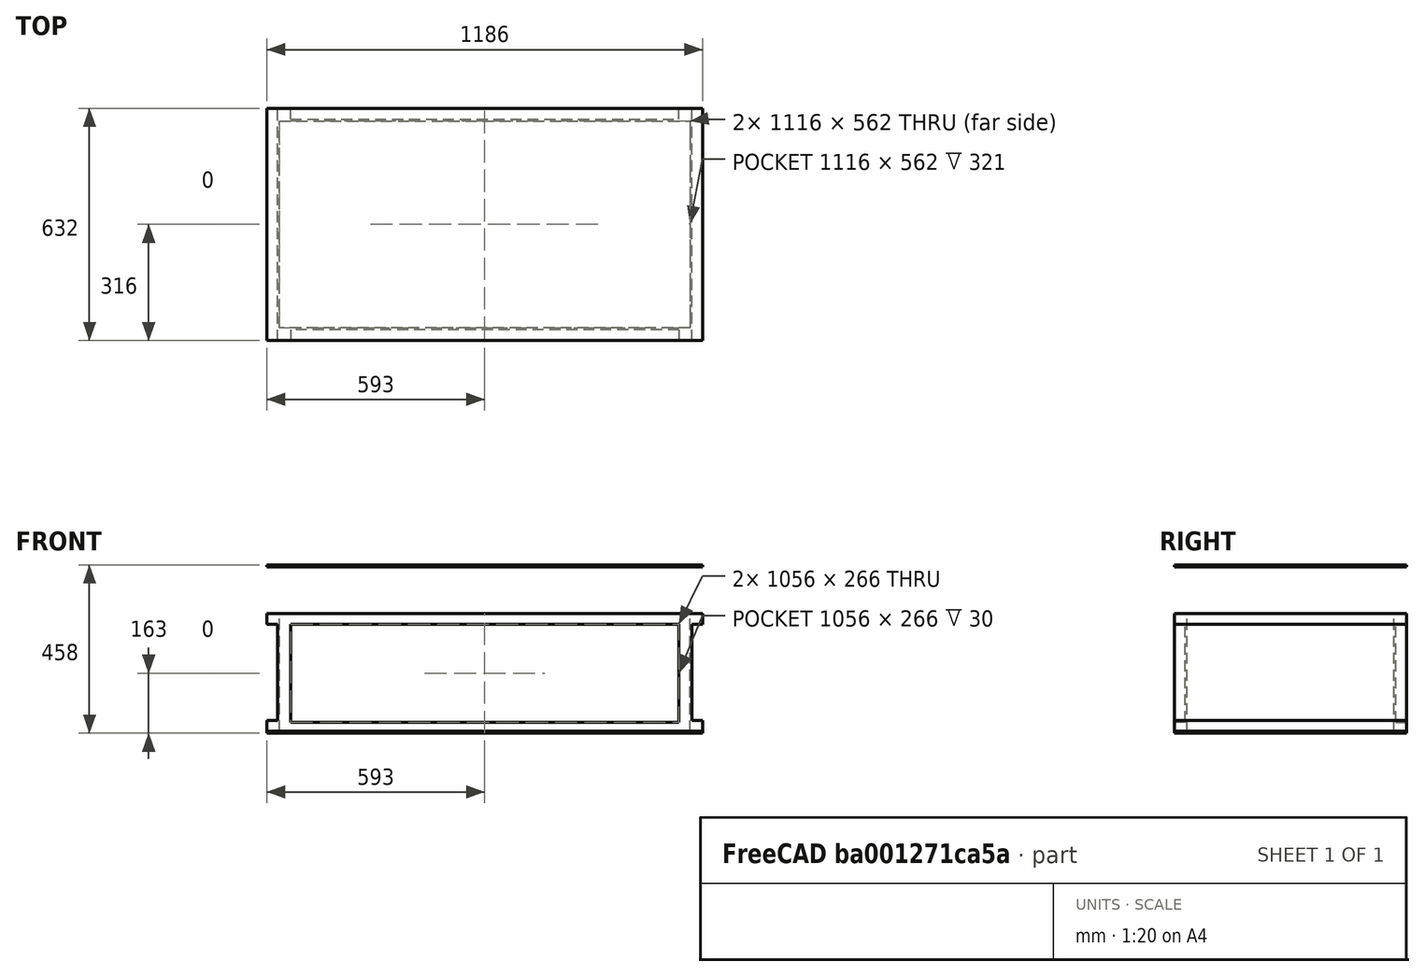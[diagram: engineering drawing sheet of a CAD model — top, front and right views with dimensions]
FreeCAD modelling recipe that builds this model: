
FCSTD DOCUMENT  (FreeCAD 0.20R)
Label: boite_lightcon_C231999
License: All rights reserved
LicenseURL: http://en.wikipedia.org/wiki/All_rights_reserved
objects: TechDraw::DrawViewDimension×11, Sketcher::SketchObject×5, PartDesign::Pocket×3, PartDesign::Pad×2, PartDesign::Mirrored×2, PartDesign::Body×2, TechDraw::DrawViewPart×2, TechDraw::DrawViewSection×2, Spreadsheet::Sheet×1, TechDraw::DrawSVGTemplate×1, PartDesign::Plane×1, Part::FeaturePython×1, TechDraw::DrawPage×1
note: 21 computed .brp shape members not serialized (recipe doc carries the construction recipe); baked Part::Feature solids carry a one-line shape summary decoded from their .brp

FEATURE [Sketcher::SketchObject] Sketch  label="extBox"
  FullyConstrained = true
  MapMode = 5
  Support = -> [XY_Plane]
  expr: Constraints[8] = Spreadsheet.extboxwidth
  expr: Constraints[9] = Spreadsheet.extboxlength
  sketch-geometry (4):
    g0: LineSegment StartX=-593 StartY=316 StartZ=0 EndX=593 EndY=316 EndZ=0
    g1: LineSegment StartX=593 StartY=316 StartZ=0 EndX=593 EndY=-316 EndZ=0
    g2: LineSegment StartX=593 StartY=-316 StartZ=0 EndX=-593 EndY=-316 EndZ=0
    g3: LineSegment StartX=-593 StartY=-316 StartZ=0 EndX=-593 EndY=316 EndZ=0
  constraints (10):
    c: Coincident(g0,g1)
    c: Coincident(g1,g2)
    c: Coincident(g2,g3)
    c: Coincident(g3,g0)
    c: Horizontal(g2)
    c: Vertical(g3)
    c: Symmetric(g0,g0,g-2)
    c: Symmetric(g0,g1,g-1)
    c: DistanceY(g3,g3) = 632
    c: DistanceX(g0,g0) = 1186
FEATURE [Spreadsheet::Sheet] Spreadsheet  label="dim"
  cells = A1=Braces thick; B1(Bracesthick)==30mm; A2=panel thick; B2(panelthick)==5mm; A3=ext box height; B3(extboxheight)==326mm; A4=ext box length; B4(extboxlength)==1186mm; A5=int box width; B5(intboxwidth)==562mm; A6=int box height; B6(intboxheight)==extboxheight - panelthick; A7=ext box width; B7(extboxwidth)==intboxwidth + 2 * panelthick + 2 * Bracesthick; A8=int box length; B8(intboxlength)==extboxlength - 2 * Bracesthick - 2 * panelthick
FEATURE [PartDesign::Pad] Pad
  Direction = (0,0,1)
  Length = 326
  Length2 = 10
  Profile = -> Sketch
  ReferenceAxis = -> Sketch [N_Axis]
  Type = 0
  expr: Length = Spreadsheet.extboxheight
FEATURE [Sketcher::SketchObject] Sketch001
  FullyConstrained = true
  MapMode = 5
  Placement = pos=(0,0,0) rot=(1,0,0;1.5708rad)
  Support = -> [XZ_Plane]
  expr: Constraints[10] = Spreadsheet.extboxlength / 2
  expr: Constraints[11] = Spreadsheet.Bracesthick
  expr: Constraints[8] = Spreadsheet.extboxheight - Spreadsheet.panelthick - 2 * Spreadsheet.Bracesthick
  expr: Constraints[9] = Spreadsheet.panelthick + Spreadsheet.Bracesthick
  sketch-geometry (4):
    g0: LineSegment StartX=563 StartY=296 StartZ=0 EndX=593 EndY=296 EndZ=0
    g1: LineSegment StartX=593 StartY=296 StartZ=0 EndX=593 EndY=35 EndZ=0
    g2: LineSegment StartX=593 StartY=35 StartZ=0 EndX=563 EndY=35 EndZ=0
    g3: LineSegment StartX=563 StartY=35 StartZ=0 EndX=563 EndY=296 EndZ=0
  constraints (12):
    c: Coincident(g0,g1)
    c: Coincident(g1,g2)
    c: Coincident(g2,g3)
    c: Coincident(g3,g0)
    c: Horizontal(g0)
    c: Horizontal(g2)
    c: Vertical(g1)
    c: Vertical(g3)
    c: DistanceY(g3,g3) = 261
    c: DistanceY(g-1,g2) = 35
    c: DistanceX(g-1,g0) = 593
    c: DistanceX(g0,g0) = 30
FEATURE [PartDesign::Pocket] Pocket
  BaseFeature = -> Pad
  Direction = (0,1,-2e-16)
  Length = 5
  Length2 = 5
  Midplane = true
  Profile = -> Sketch001
  ReferenceAxis = -> Sketch001 [N_Axis]
  Type = 1
FEATURE [PartDesign::Mirrored] Mirrored
  BaseFeature = -> Pocket
  MirrorPlane = -> Sketch001 [V_Axis]
  Originals = -> [Pocket]
FEATURE [Sketcher::SketchObject] Sketch002
  AttachmentOffset = pos=(0,0,286) rot=(0,0,1;0rad)
  FullyConstrained = true
  MapMode = 5
  Placement = pos=(0,-286,6.35e-14) rot=(1,0,0;1.5708rad)
  Support = -> [XZ_Plane]
  expr: .AttachmentOffset.Base.z = 0.5 * <<dim>>.extboxwidth - <<dim>>.Bracesthick
  expr: Constraints[16] = <<dim>>.extboxheight
  expr: Constraints[17] = <<dim>>.extboxlength
  expr: Constraints[18] = 2 * <<dim>>.Bracesthick + <<dim>>.panelthick
  expr: Constraints[19] = <<dim>>.Bracesthick
  expr: Constraints[21] = <<dim>>.extboxheight - 2 * <<dim>>.Bracesthick
  sketch-geometry (8):
    g0: LineSegment StartX=-528 StartY=296 StartZ=0 EndX=528 EndY=296 EndZ=0
    g1: LineSegment StartX=528 StartY=296 StartZ=0 EndX=528 EndY=30 EndZ=0
    g2: LineSegment StartX=528 StartY=30 StartZ=0 EndX=-528 EndY=30 EndZ=0
    g3: LineSegment StartX=-528 StartY=30 StartZ=0 EndX=-528 EndY=296 EndZ=0
    g4: LineSegment StartX=-593 StartY=326 StartZ=0 EndX=593 EndY=326 EndZ=0
    g5: LineSegment StartX=593 StartY=326 StartZ=0 EndX=593 EndY=0 EndZ=0
    g6: LineSegment StartX=593 StartY=0 StartZ=0 EndX=-593 EndY=0 EndZ=0
    g7: LineSegment StartX=-593 StartY=0 StartZ=0 EndX=-593 EndY=326 EndZ=0
  constraints (22):
    c: Coincident(g0,g1)
    c: Coincident(g1,g2)
    c: Coincident(g2,g3)
    c: Coincident(g3,g0)
    c: Horizontal(g2)
    c: Vertical(g1)
    c: Vertical(g3)
    c: Coincident(g4,g5)
    c: Coincident(g5,g6)
    c: Coincident(g6,g7)
    c: Coincident(g7,g4)
    c: Horizontal(g4)
    c: Vertical(g5)
    c: Vertical(g7)
    c: PointOnObject(g5,g-1)
    c: Symmetric(g5,g6,g-2)
    c: DistanceY(g6,g4) = 326
    c: DistanceX(g4,g4) = 1186
    c: DistanceX(g4,g0) = 65
    c: DistanceY(g0,g4) = 30
    c: Symmetric(g0,g0,g-2)
    c: DistanceY(g3,g3) = 266
FEATURE [PartDesign::Pocket] Pocket001
  BaseFeature = -> Mirrored
  Direction = (0,1,-2e-16)
  Length = 30
  Length2 = 5
  Profile = -> Sketch002
  ReferenceAxis = -> Sketch002 [N_Axis]
  Reversed = true
  Type = 0
  expr: Length = <<dim>>.Bracesthick
FEATURE [PartDesign::Mirrored] Mirrored001
  BaseFeature = -> Pocket001
  MirrorPlane = -> XZ_Plane
  Originals = -> [Pocket001]
FEATURE [Sketcher::SketchObject] Sketch003
  AttachmentOffset = pos=(0,0,5) rot=(0,0,1;0rad)
  FullyConstrained = true
  MapMode = 5
  Placement = pos=(0,0,5) rot=(0,0,1;0rad)
  Support = -> [XY_Plane]
  expr: .AttachmentOffset.Base.z = <<dim>>.extboxheight - <<dim>>.intboxheight
  expr: Constraints[8] = <<dim>>.intboxlength
  expr: Constraints[9] = <<dim>>.intboxwidth
  sketch-geometry (4):
    g0: LineSegment StartX=-558 StartY=281 StartZ=0 EndX=558 EndY=281 EndZ=0
    g1: LineSegment StartX=558 StartY=281 StartZ=0 EndX=558 EndY=-281 EndZ=0
    g2: LineSegment StartX=558 StartY=-281 StartZ=0 EndX=-558 EndY=-281 EndZ=0
    g3: LineSegment StartX=-558 StartY=-281 StartZ=0 EndX=-558 EndY=281 EndZ=0
  constraints (10):
    c: Coincident(g0,g1)
    c: Coincident(g1,g2)
    c: Coincident(g2,g3)
    c: Coincident(g3,g0)
    c: Horizontal(g2)
    c: Vertical(g3)
    c: Symmetric(g0,g0,g-2)
    c: Symmetric(g0,g1,g-1)
    c: DistanceX(g0,g0) = 1116
    c: DistanceY(g3,g3) = 562
FEATURE [PartDesign::Pocket] Pocket002
  BaseFeature = -> Mirrored001
  Direction = (0,0,-1)
  Length = 5
  Length2 = 5
  Profile = -> Sketch003
  ReferenceAxis = -> Sketch003 [N_Axis]
  Reversed = true
  Type = 1
FEATURE [Sketcher::SketchObject] Sketch004
  FullyConstrained = true
  MapMode = 5
  Support = -> [XY_Plane001]
  expr: Constraints[8] = <<dim>>.extboxlength
  expr: Constraints[9] = <<dim>>.extboxwidth
  sketch-geometry (4):
    g0: LineSegment StartX=-593 StartY=316 StartZ=0 EndX=593 EndY=316 EndZ=0
    g1: LineSegment StartX=593 StartY=316 StartZ=0 EndX=593 EndY=-316 EndZ=0
    g2: LineSegment StartX=593 StartY=-316 StartZ=0 EndX=-593 EndY=-316 EndZ=0
    g3: LineSegment StartX=-593 StartY=-316 StartZ=0 EndX=-593 EndY=316 EndZ=0
  constraints (10):
    c: Coincident(g0,g1)
    c: Coincident(g1,g2)
    c: Coincident(g2,g3)
    c: Coincident(g3,g0)
    c: Horizontal(g2)
    c: Vertical(g3)
    c: Symmetric(g0,g0,g-2)
    c: Symmetric(g0,g1,g-1)
    c: DistanceX(g0,g0) = 1186
    c: DistanceY(g3,g3) = 632
FEATURE [PartDesign::Pad] Pad001
  Direction = (0,0,1)
  Length = 5
  Length2 = 10
  Profile = -> Sketch004
  ReferenceAxis = -> Sketch004 [N_Axis]
  Type = 0
  expr: Length = <<dim>>.panelthick
FEATURE [PartDesign::Body] Body001  label="TopPanel"
  Group = -> [Sketch004,Pad001]
  Origin = -> Origin001
  Placement = pos=(0,0,453) rot=(0,0,1;0rad)
  Tip = -> Pad001
FEATURE [TechDraw::DrawSVGTemplate] Template
  EditableTexts = Drawing_number=1; FC-Date=2025-02-07; FC-SC=1:10; FC-SH=1; FC-Title=Boite C231999
  Height = 210
  Orientation = 1
  Width = 297
FEATURE [PartDesign::Plane] DatumPlane  label="floor"
  AttachmentOffset = pos=(0,0,5) rot=(0,0,1;0rad)
  Length = 1170.62
  MapMode = 2
  Placement = pos=(0,0,5) rot=(0,0,1;0rad)
  ResizeMode = 0
  Support = -> [XY_Plane]
  Width = 425.615
  expr: .AttachmentOffset.Base.z = <<dim>>.panelthick
FEATURE [PartDesign::Body] Body
  Group = -> [Sketch,Pad,Sketch001,Pocket,Mirrored,Sketch002,Pocket001,Mirrored001,Sketch003,Pocket002,DatumPlane]
  Origin = -> Origin
  Tip = -> Pocket002
FEATURE [Part::FeaturePython] Slice  # WARN: FeaturePython — macro-defined, semantics opaque (R4)
  Base = -> Pocket002
  Mode = 1
  Tolerance = 0
  Tools = -> [DatumPlane]
FEATURE [TechDraw::DrawViewPart] View  label="Side"
  CoarseView = false
  Direction = (0,1,0)
  Focus = 100
  HardHidden = false
  IsoCount = 0
  IsoHidden = false
  IsoVisible = false
  LockPosition = false
  Perspective = false
  Rotation = 0
  Scale = 0.1
  ScaleType = 0
  SeamHidden = false
  SeamVisible = true
  SmoothHidden = false
  SmoothVisible = true
  Source = -> [Slice,Body001]
  X = 211.427
  XDirection = (-1,0,0)
  Y = 169.483
FEATURE [TechDraw::DrawViewPart] View001  label="Front"
  CoarseView = false
  Direction = (-1,0,0)
  Focus = 100
  HardHidden = false
  IsoCount = 0
  IsoHidden = false
  IsoVisible = false
  LockPosition = false
  Perspective = false
  Rotation = 0
  Scale = 0.1
  ScaleType = 0
  SeamHidden = false
  SeamVisible = true
  SmoothHidden = false
  SmoothVisible = true
  Source = -> [Slice,Body001]
  X = 71.9398
  XDirection = (0,-1,0)
  Y = 152.626
FEATURE [TechDraw::DrawViewSection] SectionView  label="Section A - A"
  BaseView = -> View
  CoarseView = false
  CutSurfaceDisplay = 2
  Direction = (0,0,1)
  FileGeomPattern = <path>
  FileHatchPattern = <path>
  Focus = 100
  FuseBeforeCut = false
  HardHidden = false
  HatchScale = 1
  IsoCount = 0
  IsoHidden = false
  IsoVisible = false
  LockPosition = false
  NameGeomPattern = Diamond
  Perspective = false
  Rotation = 0
  Scale = 0.1
  ScaleType = 0
  SeamHidden = false
  SeamVisible = true
  SectionDirection = 3
  SectionNormal = (0,0,1)
  SectionOrigin = (0,0,229)
  SectionSymbol = A
  SmoothHidden = false
  SmoothVisible = true
  Source = -> [Slice,Body001]
  X = 75.6812
  XDirection = (-1,0,0)
  Y = 56.9049
FEATURE [TechDraw::DrawViewSection] SectionView001  label="Section B - B"
  BaseView = -> View001
  CoarseView = false
  CutSurfaceDisplay = 2
  Direction = (0,-1,0)
  FileGeomPattern = <path>
  FileHatchPattern = <path>
  Focus = 100
  FuseBeforeCut = false
  HardHidden = false
  HatchScale = 1
  IsoCount = 0
  IsoHidden = false
  IsoVisible = false
  LockPosition = false
  NameGeomPattern = Diamond
  Perspective = false
  Rotation = 0
  Scale = 0.1
  ScaleType = 0
  SeamHidden = false
  SeamVisible = true
  SectionDirection = 1
  SectionNormal = (0,-1,0)
  SectionOrigin = (0,0,229)
  SectionSymbol = B
  SmoothHidden = false
  SmoothVisible = true
  Source = -> [Slice,Body001]
  X = 210.78
  XDirection = (1,0,0)
  Y = 101.213
FEATURE [TechDraw::DrawViewDimension] Dimension
  AngleOverride = false
  Arbitrary = false
  ArbitraryTolerances = false
  EqualTolerance = true
  ExtensionAngle = 0
  FormatSpec = %.2w
  FormatSpecOverTolerance = %+.2w
  FormatSpecUnderTolerance = %+.2w
  Inverted = false
  LineAngle = 0
  LockPosition = false
  MeasureType = 1
  OverTolerance = 0
  References2D = -> [View001]
  Rotation = 0
  Scale = 0.1
  ScaleType = 0
  TheoreticalExact = false
  Type = 2
  UnderTolerance = 0
  X = 38.436
  Y = -6.51768
FEATURE [TechDraw::DrawViewDimension] Dimension001
  AngleOverride = false
  Arbitrary = false
  ArbitraryTolerances = false
  EqualTolerance = true
  ExtensionAngle = 0
  FormatSpec = %.2w
  FormatSpecOverTolerance = %+.2w
  FormatSpecUnderTolerance = %+.2w
  Inverted = false
  LineAngle = 0
  LockPosition = false
  MeasureType = 1
  OverTolerance = 0
  References2D = -> [View001]
  Rotation = 0
  Scale = 0.1
  ScaleType = 0
  TheoreticalExact = false
  Type = 2
  UnderTolerance = 0
  X = -44.7707
  Y = -19.3044
FEATURE [TechDraw::DrawViewDimension] Dimension002
  AngleOverride = false
  Arbitrary = false
  ArbitraryTolerances = false
  EqualTolerance = true
  ExtensionAngle = 0
  FormatSpec = %.2w
  FormatSpecOverTolerance = %+.2w
  FormatSpecUnderTolerance = %+.2w
  Inverted = false
  LineAngle = 0
  LockPosition = false
  MeasureType = 1
  OverTolerance = 0
  References2D = -> [View001]
  Rotation = 0
  Scale = 0.1
  ScaleType = 0
  TheoreticalExact = false
  Type = 2
  UnderTolerance = 0
  X = -40.294
  Y = 5.50745
FEATURE [TechDraw::DrawViewDimension] Dimension003
  AngleOverride = false
  Arbitrary = false
  ArbitraryTolerances = false
  EqualTolerance = true
  ExtensionAngle = 0
  FormatSpec = %.2w
  FormatSpecOverTolerance = %+.2w
  FormatSpecUnderTolerance = %+.2w
  Inverted = false
  LineAngle = 0
  LockPosition = false
  MeasureType = 1
  OverTolerance = 0
  References2D = -> [View001]
  Rotation = 0
  Scale = 0.1
  ScaleType = 0
  TheoreticalExact = false
  Type = 1
  UnderTolerance = 0
  X = -16.4507
  Y = -2.58227
FEATURE [TechDraw::DrawViewDimension] Dimension004
  AngleOverride = false
  Arbitrary = false
  ArbitraryTolerances = false
  EqualTolerance = true
  ExtensionAngle = 0
  FormatSpec = %.2w
  FormatSpecOverTolerance = %+.2w
  FormatSpecUnderTolerance = %+.2w
  Inverted = false
  LineAngle = 0
  LockPosition = false
  MeasureType = 1
  OverTolerance = 0
  References2D = -> [View001]
  Rotation = 0
  Scale = 0.1
  ScaleType = 0
  TheoreticalExact = false
  Type = 1
  UnderTolerance = 0
  X = -9.60366
  Y = 30.607
FEATURE [TechDraw::DrawViewDimension] Dimension005
  AngleOverride = false
  Arbitrary = false
  ArbitraryTolerances = false
  EqualTolerance = true
  ExtensionAngle = 0
  FormatSpec = %.2w
  FormatSpecOverTolerance = %+.2w
  FormatSpecUnderTolerance = %+.2w
  Inverted = false
  LineAngle = 0
  LockPosition = false
  MeasureType = 1
  OverTolerance = 0
  References2D = -> [View]
  Rotation = 0
  Scale = 0.1
  ScaleType = 0
  TheoreticalExact = false
  Type = 1
  UnderTolerance = 0
  X = -18.6738
  Y = -23.8024
FEATURE [TechDraw::DrawViewDimension] Dimension006
  AngleOverride = false
  Arbitrary = false
  ArbitraryTolerances = false
  EqualTolerance = true
  ExtensionAngle = 0
  FormatSpec = %.2w
  FormatSpecOverTolerance = %+.2w
  FormatSpecUnderTolerance = %+.2w
  Inverted = false
  LineAngle = 0
  LockPosition = false
  MeasureType = 1
  OverTolerance = 0
  References2D = -> [View]
  Rotation = 0
  Scale = 0.1
  ScaleType = 0
  TheoreticalExact = false
  Type = 1
  UnderTolerance = 0
  X = -38.6814
  Y = 18.3357
FEATURE [TechDraw::DrawViewDimension] Dimension007
  AngleOverride = false
  Arbitrary = false
  ArbitraryTolerances = false
  EqualTolerance = true
  ExtensionAngle = 0
  FormatSpec = %.2w
  FormatSpecOverTolerance = %+.2w
  FormatSpecUnderTolerance = %+.2w
  Inverted = false
  LineAngle = 0
  LockPosition = false
  MeasureType = 1
  OverTolerance = 0
  References2D = -> [SectionView001]
  Rotation = 0
  Scale = 0.1
  ScaleType = 0
  TheoreticalExact = false
  Type = 2
  UnderTolerance = 0
  X = -32.2592
  Y = -3.64706
FEATURE [TechDraw::DrawViewDimension] Dimension008
  AngleOverride = false
  Arbitrary = false
  ArbitraryTolerances = false
  EqualTolerance = true
  ExtensionAngle = 0
  FormatSpec = %.2w
  FormatSpecOverTolerance = %+.2w
  FormatSpecUnderTolerance = %+.2w
  Inverted = false
  LineAngle = 0
  LockPosition = false
  MeasureType = 1
  OverTolerance = 0
  References2D = -> [SectionView001]
  Rotation = 0
  Scale = 0.1
  ScaleType = 0
  TheoreticalExact = false
  Type = 1
  UnderTolerance = 0
  X = 1.6235
  Y = -10.3619
FEATURE [TechDraw::DrawViewDimension] Dimension009
  AngleOverride = false
  Arbitrary = false
  ArbitraryTolerances = false
  EqualTolerance = true
  ExtensionAngle = 0
  FormatSpec = %.2w
  FormatSpecOverTolerance = %+.2w
  FormatSpecUnderTolerance = %+.2w
  Inverted = false
  LineAngle = 0
  LockPosition = false
  MeasureType = 1
  OverTolerance = 0
  References2D = -> [SectionView]
  Rotation = 0
  Scale = 0.1
  ScaleType = 0
  TheoreticalExact = false
  Type = 2
  UnderTolerance = 0
  X = 41.3481
  Y = -7.2815
FEATURE [TechDraw::DrawViewDimension] Dimension010
  AngleOverride = false
  Arbitrary = false
  ArbitraryTolerances = false
  EqualTolerance = true
  ExtensionAngle = 0
  FormatSpec = %.2w
  FormatSpecOverTolerance = %+.2w
  FormatSpecUnderTolerance = %+.2w
  Inverted = false
  LineAngle = 0
  LockPosition = false
  MeasureType = 1
  OverTolerance = 0
  References2D = -> [View001]
  Rotation = 0
  Scale = 0.1
  ScaleType = 0
  TheoreticalExact = false
  Type = 2
  UnderTolerance = 0
  X = 37.0287
  Y = 18.9458
FEATURE [TechDraw::DrawPage] Page
  KeepUpdated = true
  NextBalloonIndex = 1
  ProjectionType = 0
  Scale = 0.1
  Template = -> Template
  Views = -> [View,View001,SectionView,SectionView001,Dimension,Dimension001,Dimension002,Dimension003,Dimension004,Dimension005,Dimension006,Dimension007,Dimension008,Dimension009,Dimension010]
note: 4 file-system paths scrubbed to <path> (originals preserved in the JSON sidecar)
